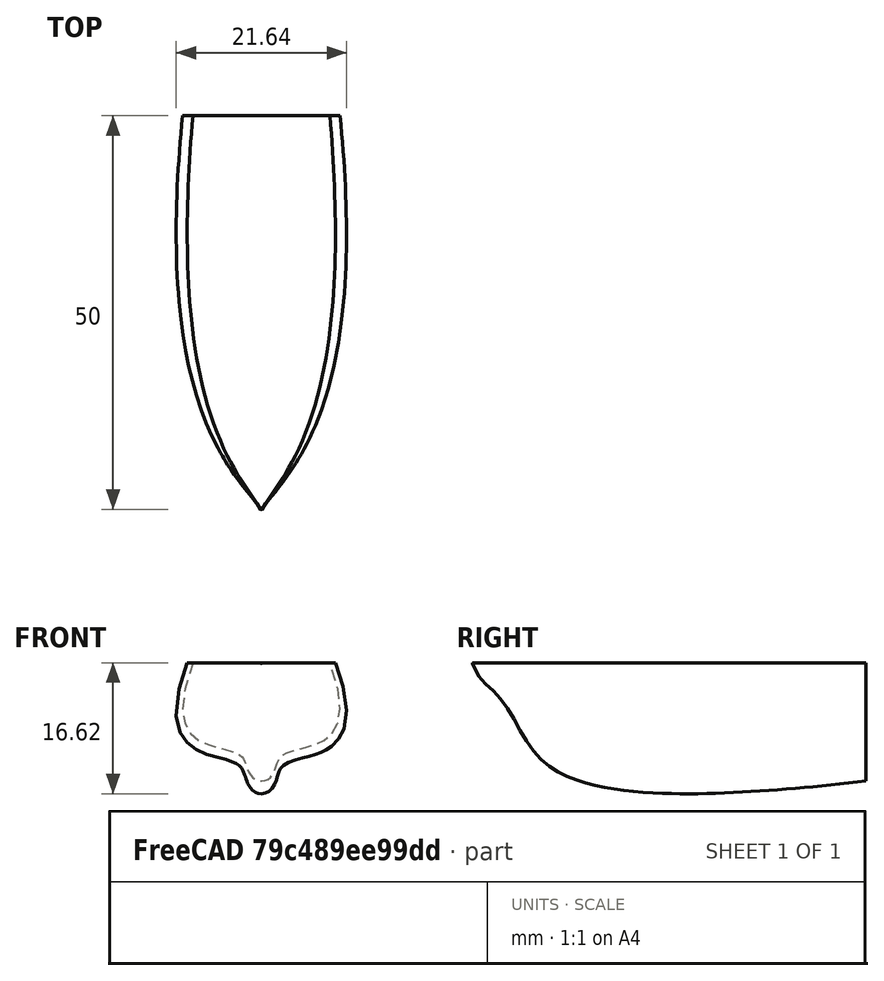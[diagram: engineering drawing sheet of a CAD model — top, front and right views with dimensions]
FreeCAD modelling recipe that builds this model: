
FCSTD DOCUMENT  (FreeCAD 1.0R39285 (Git))
Label: boat_loft
License: All rights reserved
LicenseURL: https://en.wikipedia.org/wiki/All_rights_reserved
objects: Sketcher::SketchObject×4, PartDesign::Body×1, Part::FeaturePython×1
note: 10 computed .brp shape members not serialized (recipe doc carries the construction recipe); baked Part::Feature solids carry a one-line shape summary decoded from their .brp

FEATURE [Sketcher::SketchObject] Sketch  label="hull_stern"
  ArcFitTolerance = 1e-06
  AttachmentOffset = pos=(0,0,-25) rot=(0,0,1;0rad)
  AttachmentSupport = -> [XZ_Plane]
  FullyConstrained = false
  MakeInternals = false
  MapMode = 5
  Placement = pos=(0,25,-5.6e-15) rot=(1,0,0;1.5708rad)
  sketch-geometry (23):
    g0-g5: Circle [constr] x6 (B-spline internal-alignment scaffolding for g6; pole/knot coordinates omitted)
    g6: BSplineCurve PolesCount=6 KnotsCount=4 Degree=3 IsPeriodic=0
    g7-g10: GeomPoint [constr] x4 (B-spline internal-alignment scaffolding for g6; pole/knot coordinates omitted)
    g11-g16: Circle [constr] x6 (B-spline internal-alignment scaffolding for g17; pole/knot coordinates omitted)
    g17: BSplineCurve PolesCount=6 KnotsCount=4 Degree=3 IsPeriodic=0
    g18-g21: GeomPoint [constr] x4 (B-spline internal-alignment scaffolding for g17; pole/knot coordinates omitted)
    g22: LineSegment StartX=-10 StartY=0 StartZ=0 EndX=10 EndY=0 EndZ=0
  constraints (16):
    c: Weight(g0) = 1
    c: Equal(g0, g1-g5) x5
    c: InternalAlignment(g0-g5 -> g6) x6
    c: InternalAlignment(g7-g10 -> g6) x4
    c: PointOnObject(g0,g-1)
    c: PointOnObject(g5,g-2)
    c: Horizontal(g4,g6)
    c: DistanceX(g6,g-1) = 10
    c: DistanceY(g6,g-1) = 15
    c: Weight(g11) = 1
    c: Equal(g11, g12-g16) x5
    c: InternalAlignment(g11-g16 -> g17) x6
    c: InternalAlignment(g18-g21 -> g17) x4
    c: Coincident(g22,g6)
    c: Coincident(g22,g17)
    c: Horizontal(g22)
FEATURE [Sketcher::SketchObject] Sketch001  label="hull_bow"
  ArcFitTolerance = 1e-06
  AttachmentOffset = pos=(0,0,25) rot=(0,0,1;0rad)
  AttachmentSupport = -> [XZ_Plane]
  FullyConstrained = true
  MakeInternals = false
  MapMode = 5
  Placement = pos=(0,-25,5.6e-15) rot=(1,0,0;1.5708rad)
  sketch-geometry (4):
    g0: ArcOfCircle CenterX=0 CenterY=0 CenterZ=0 NormalX=0 NormalY=0 NormalZ=1 AngleXU=0 Radius=0.1 StartAngle=3.14159 EndAngle=6.28319
    g1: LineSegment StartX=-0.1 StartY=0 StartZ=0 EndX=0.1 EndY=0 EndZ=0
    g2: LineSegment StartX=-0.1 StartY=0 StartZ=0 EndX=0.1 EndY=0 EndZ=0
    g3: LineSegment StartX=-0.1 StartY=0 StartZ=0 EndX=0.1 EndY=0 EndZ=0
  constraints (10):
    c: Coincident(g0,g-1)
    c: Radius(g0) = 0.1
    c: Coincident(g1,g0)
    c: Coincident(g1,g0)
    c: Coincident(g2,g0)
    c: Coincident(g2,g0)
    c: Coincident(g3,g0)
    c: Coincident(g3,g0)
    c: Horizontal(g3)
    c: PointOnObject(g0,g1)
FEATURE [Sketcher::SketchObject] Sketch002  label="hull_xy"
  ArcFitTolerance = 1e-06
  AttachmentSupport = -> [XY_Plane]
  ExternalGeometry = -> [Sketch,Sketch001]
  FullyConstrained = false
  MakeInternals = false
  MapMode = 5
  sketch-geometry (14):
    g0-g3: Circle [constr] x4 (B-spline internal-alignment scaffolding for g4; pole/knot coordinates omitted)
    g4: BSplineCurve PolesCount=4 KnotsCount=2 Degree=3 IsPeriodic=0
    g5: GeomPoint [constr] X=-10 Y=25 Z=0
    g6: GeomPoint [constr] X=-0.1 Y=-25 Z=0
    g7-g10: Circle [constr] x4 (B-spline internal-alignment scaffolding for g11; pole/knot coordinates omitted)
    g11: BSplineCurve PolesCount=4 KnotsCount=2 Degree=3 IsPeriodic=0
    g12: GeomPoint [constr] X=10 Y=25 Z=0
    g13: GeomPoint [constr] X=0.1 Y=-25 Z=0
  constraints (18):
    c: Weight(g0) = 1
    c: Equal(g0,g1)
    c: Equal(g0,g2)
    c: Equal(g0,g3)
    c: InternalAlignment(g0-g3 -> g4) x4
    c: InternalAlignment(g5,g4)
    c: InternalAlignment(g6,g4)
    c: Coincident(g0,g-3)
    c: Coincident(g3,g-4)
    c: Weight(g7) = 1
    c: Equal(g7,g8)
    c: Equal(g7,g9)
    c: Equal(g7,g10)
    c: InternalAlignment(g7-g10 -> g11) x4
    c: InternalAlignment(g12,g11)
    c: InternalAlignment(g13,g11)
    c: Coincident(g11,g-3)
    c: Coincident(g11,g-4)
FEATURE [Sketcher::SketchObject] Sketch003  label="hull_yz"
  ArcFitTolerance = 1e-06
  AttachmentSupport = -> [YZ_Plane]
  ExternalGeometry = -> [Sketch,Sketch001]
  FullyConstrained = false
  MakeInternals = false
  MapMode = 5
  Placement = pos=(0,0,0) rot=(0.57735,0.57735,0.57735;2.0944rad)
  sketch-geometry (10):
    g0: Circle [constr] CenterX=25 CenterY=-15 CenterZ=0 NormalX=0 NormalY=0 NormalZ=1 AngleXU=0 Radius=1
    g1: Circle [constr] CenterX=-25 CenterY=-0.1 CenterZ=0 NormalX=0 NormalY=0 NormalZ=1 AngleXU=0 Radius=1
    g2: BSplineCurve PolesCount=5 KnotsCount=3 Degree=3 IsPeriodic=0
    g3: GeomPoint [constr] X=25 Y=-15 Z=0
    g4: GeomPoint [constr] X=-25 Y=-0.1 Z=0
    g5: Circle [constr] CenterX=-25.1516 CenterY=-20.9217 CenterZ=0 NormalX=0 NormalY=0 NormalZ=1 AngleXU=0 Radius=1
    g6: Circle [constr] CenterX=-13.703 CenterY=-8.42821 CenterZ=0 NormalX=0 NormalY=0 NormalZ=1 AngleXU=0 Radius=1
    g7: Circle [constr] CenterX=-25 CenterY=-1.48639 CenterZ=0 NormalX=0 NormalY=0 NormalZ=1 AngleXU=0 Radius=1
    g8: GeomPoint [constr] X=-23.6026 Y=-2.43082 Z=0
    g9: LineSegment StartX=-25 StartY=0 StartZ=0 EndX=25.0049 EndY=0 EndZ=0
  constraints (18):
    c: Weight(g0) = 1
    c: Equal(g0,g1)
    c: InternalAlignment(g0,g2)
    c: InternalAlignment(g1,g2)
    c: InternalAlignment(g3,g2)
    c: InternalAlignment(g4,g2)
    c: Coincident(g0,g-3)
    c: Coincident(g1,g-4)
    c: InternalAlignment(g5,g2)
    c: Equal(g5,g0)
    c: InternalAlignment(g6,g2)
    c: Equal(g6,g0)
    c: InternalAlignment(g7,g2)
    c: Equal(g7,g0)
    c: InternalAlignment(g8,g2)
    c: Vertical(g2,g7)
    c: Coincident(g9,g-4)
    c: Horizontal(g9)
FEATURE [PartDesign::Body] Body
  AllowCompound = false
  Group = -> [Sketch,Sketch001,Sketch002,Sketch003]
  Origin = -> Origin
FEATURE [Part::FeaturePython] CurvedArray  # WARN: FeaturePython — macro-defined, semantics opaque (R4)
  Axis = (0,1,0)
  Base = -> Sketch
  Distribution = 0
  DistributionReverse = false
  Hullcurves = -> [Sketch002,Sketch003]
  Items = 30
  KeepBase = 0
  LoftMaxDegree = 5
  MaxLoftSize = 16
  OffsetEnd = 0
  OffsetStart = 0
  Solid = true
  Surface = false
  Twist = 0
